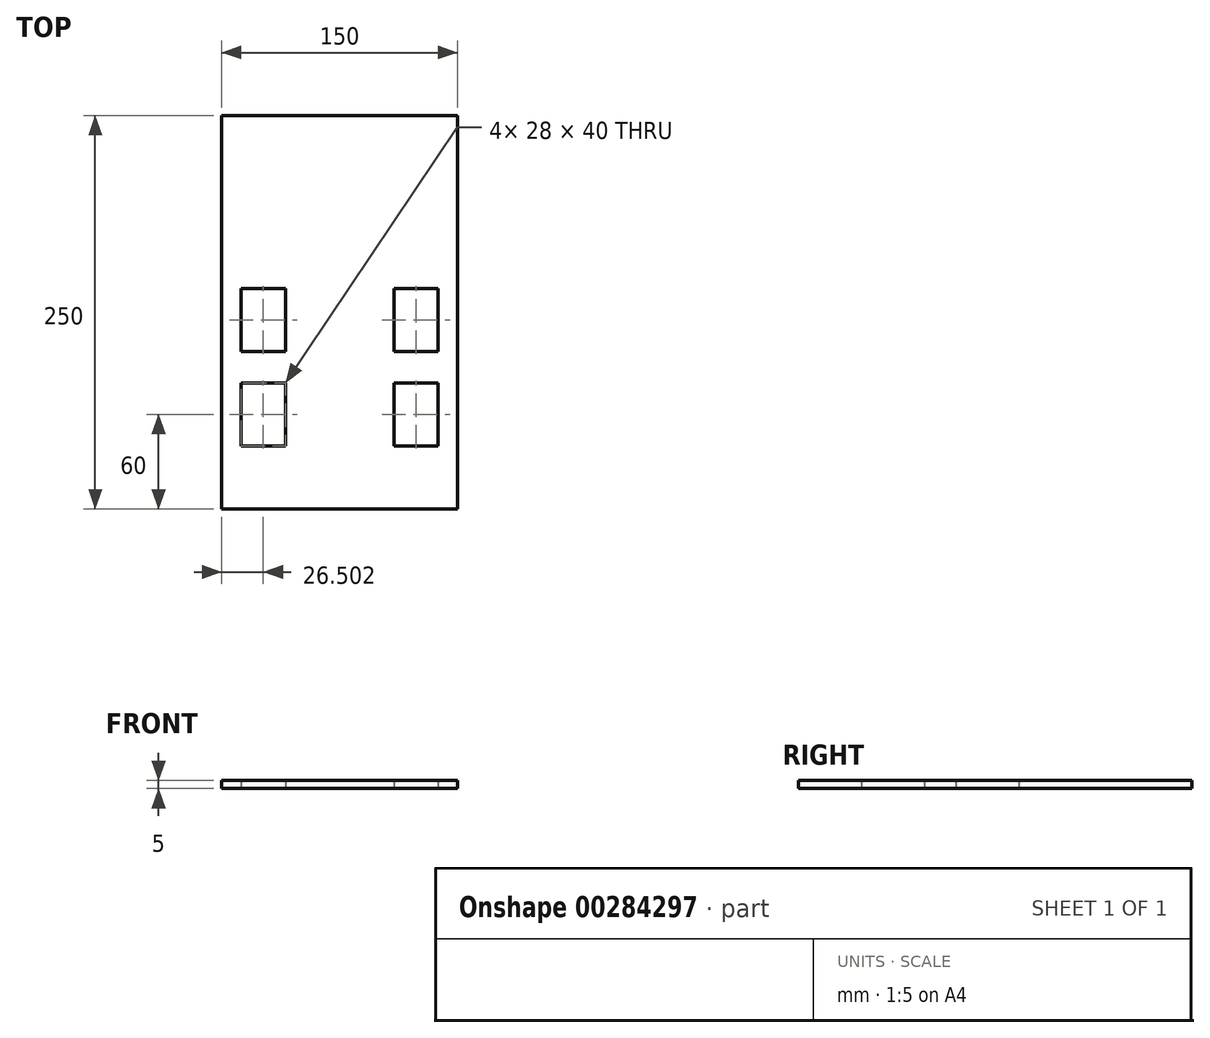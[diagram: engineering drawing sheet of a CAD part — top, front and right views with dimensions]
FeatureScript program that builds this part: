
annotation { "Feature Type Name" : "Feature", "Feature Type Description" : "" }
export const myFeature = defineFeature(function(context is Context, id is Id, definition is map)
    precondition{}
    {
        {
            var Q0;
            Q0=qCreatedBy(makeId("Top.planeOp"),FACE);
            var sketch = newSketch(context, id + "F0", { "sketchPlane" : qUnion([Q0])});
            skPoint(sketch, "E0.end.orphan", {"position": v(-58.89, 233.8) * mm});
            skPoint(sketch, "E1.start.orphan", {"position": v(-58.89, 206.99) * mm});
            skPoint(sketch, "E2.start.orphan", {"position": v(262.9, 233.8) * mm});
            skPoint(sketch, "E3.end.orphan", {"position": v(262.9, 180.17) * mm});
            skPoint(sketch, "E4.right.end.orphan", {"position": v(-58.89, 180.17) * mm});
            skLineSegment(sketch, "E5", {"start": v(-100.53, 59.03) * mm, "end": v(-100.53, -190.97) * mm});
            skLineSegment(sketch, "E6", {"start": v(-100.53, 59.03) * mm, "end": v(49.47, 59.03) * mm});
            skLineSegment(sketch, "E7", {"start": v(49.47, 59.03) * mm, "end": v(49.47, -190.97) * mm});
            skLineSegment(sketch, "E8", {"start": v(-100.53, -190.97) * mm, "end": v(49.47, -190.97) * mm});
            skLineSegment(sketch, "E9", {"start": v(-88.03, -150.97) * mm, "end": v(-100.53, -150.97) * mm});
            skLineSegment(sketch, "E10", {"start": v(-100.53, -150.97) * mm, "end": v(-88.03, -150.97) * mm});
            skPoint(sketch, "E11.start.orphan", {"position": v(-25.53, -190.97) * mm});
            skPoint(sketch, "E12.orphan", {"position": v(24.47, -150.97) * mm});
            skPoint(sketch, "E13.end.orphan", {"position": v(49.47, -150.97) * mm});
            skPoint(sketch, "E13.start.orphan", {"position": v(36.97, -150.97) * mm});
            skLineSegment(sketch, "E14", {"start": v(-88.03, -150.97) * mm, "end": v(-88.03, -110.97) * mm});
            skLineSegment(sketch, "E15", {"start": v(36.97, -150.97) * mm, "end": v(36.97, -110.97) * mm});
            skLineSegment(sketch, "E16", {"start": v(-88.03, -110.97) * mm, "end": v(-60.03, -110.97) * mm});
            skLineSegment(sketch, "E17", {"start": v(36.97, -110.97) * mm, "end": v(8.97, -110.97) * mm});
            skLineSegment(sketch, "E18", {"start": v(8.97, -110.97) * mm, "end": v(8.97, -150.97) * mm});
            skLineSegment(sketch, "E19", {"start": v(8.97, -150.97) * mm, "end": v(36.97, -150.97) * mm});
            skLineSegment(sketch, "E20", {"start": v(-60.03, -110.97) * mm, "end": v(-60.03, -150.97) * mm});
            skLineSegment(sketch, "E21", {"start": v(-60.03, -150.97) * mm, "end": v(-88.03, -150.97) * mm});
            skLineSegment(sketch, "E22", {"start": v(-88.03, -150.97) * mm, "end": v(-60.03, -150.97) * mm});
            skLineSegment(sketch, "E23", {"start": v(-88.03, -90.97) * mm, "end": v(-60.03, -90.97) * mm});
            skLineSegment(sketch, "E24", {"start": v(-88.03, -90.97) * mm, "end": v(-88.03, -50.97) * mm});
            skLineSegment(sketch, "E25", {"start": v(-88.03, -50.97) * mm, "end": v(-60.03, -50.97) * mm});
            skLineSegment(sketch, "E26", {"start": v(-60.03, -50.97) * mm, "end": v(-60.03, -90.97) * mm});
            skLineSegment(sketch, "E27", {"start": v(8.97, -90.97) * mm, "end": v(36.97, -90.97) * mm});
            skLineSegment(sketch, "E28", {"start": v(8.97, -90.97) * mm, "end": v(8.97, -50.97) * mm});
            skLineSegment(sketch, "E29", {"start": v(8.97, -50.97) * mm, "end": v(36.97, -50.97) * mm});
            skLineSegment(sketch, "E30", {"start": v(36.97, -50.97) * mm, "end": v(36.97, -90.97) * mm});
            skLineSegment(sketch, "E31", {"start": v(36.97, -150.97) * mm, "end": v(8.97, -150.97) * mm});
            skSolve(sketch);
        }
        {
            var Q0;
            {var subQ1=sQuery(id+"F0.wireOp",EDGE,"E6");Q0=makeQuery(id+"F0.imprint","IMPRINT",FACE,{"disambiguationData":[TD([[makeQuery(id+"F0.imprint","IMPRINT",EDGE,{"derivedFrom":subQ1}),-1.0]])]});}
            extrude(context, id + "F1", {"entities" : qUnion([Q0]), "depth" : 5 * mm});
        }
    });
